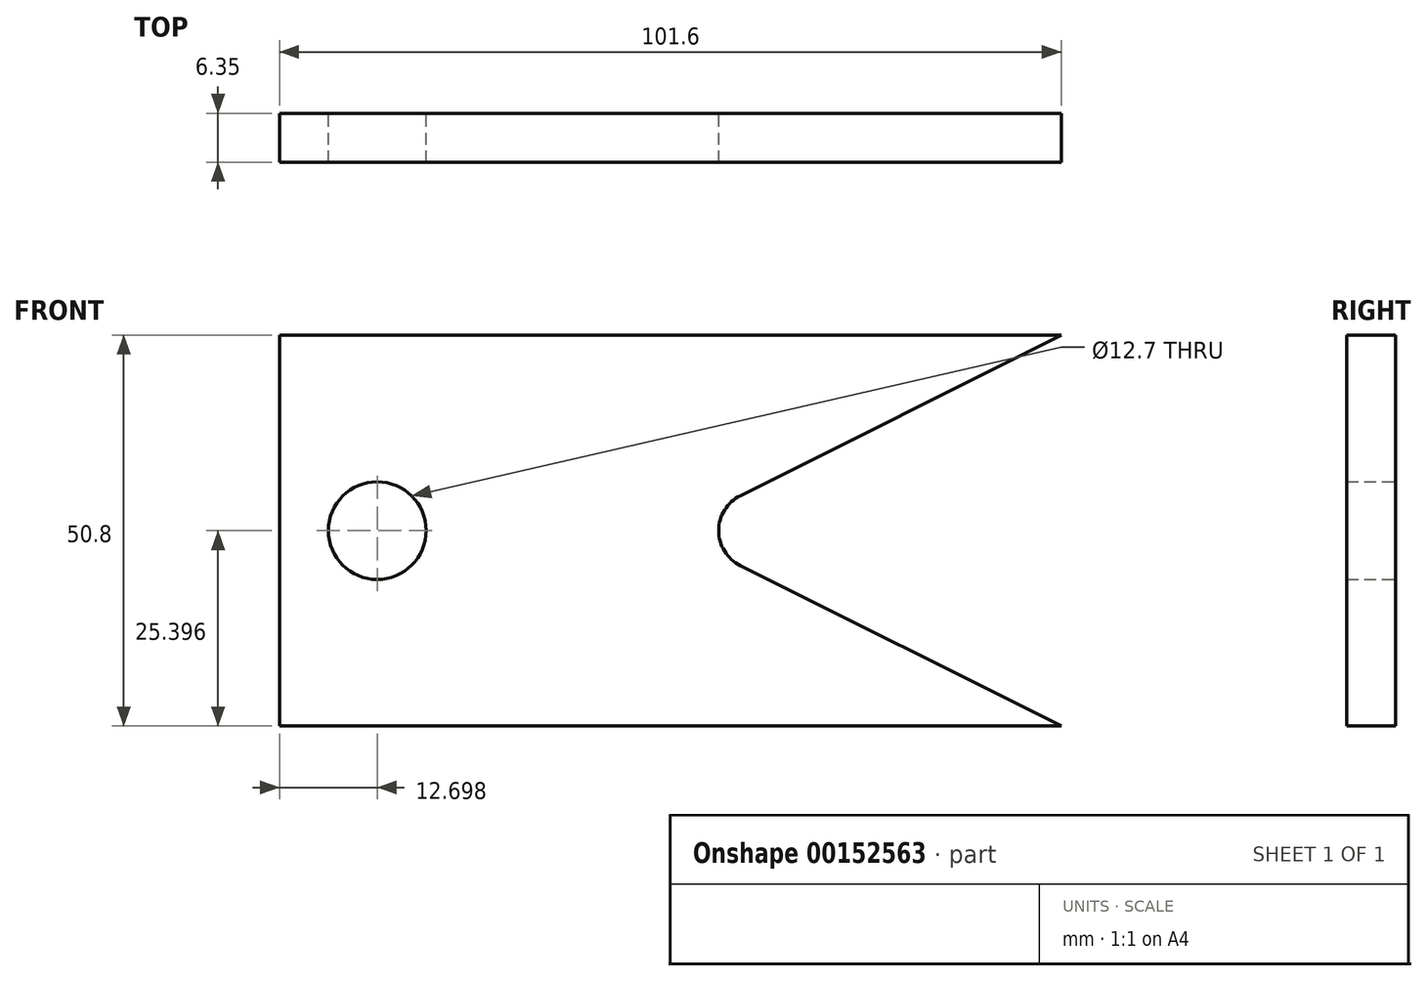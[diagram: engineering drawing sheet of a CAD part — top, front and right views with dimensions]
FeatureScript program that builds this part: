
annotation { "Feature Type Name" : "Feature", "Feature Type Description" : "" }
export const myFeature = defineFeature(function(context is Context, id is Id, definition is map)
    precondition{}
    {
        {
            var Q0;
            Q0=qCreatedBy(makeId("Front.planeOp"),FACE);
            var sketch = newSketch(context, id + "F0", { "sketchPlane" : qUnion([Q0])});
            skLineSegment(sketch, "E0.bottom", {"start": v(-46.68, 28.42) * mm, "end": v(54.92, 28.42) * mm});
            skLineSegment(sketch, "E0.top", {"start": v(-46.68, -22.38) * mm, "end": v(54.92, -22.38) * mm});
            skLineSegment(sketch, "E0.left", {"start": v(-46.68, 28.42) * mm, "end": v(-46.68, -22.38) * mm});
            skLineSegment(sketch, "E1", {"start": v(4.12, 3.02) * mm, "end": v(54.92, 28.42) * mm});
            skPoint(sketch, "E1.startSnap0", {"position": v(-46.68, 3.02) * mm});
            skPoint(sketch, "E1.startSnap1", {"position": v(4.12, 28.42) * mm});
            skLineSegment(sketch, "E2", {"start": v(4.12, 3.02) * mm, "end": v(54.92, -22.38) * mm});
            skCircle(sketch, "E3", {"center": v(-33.98, 3.02) * mm, "radius": 6.35 * mm});
            skSolve(sketch);
        }
        {
            var Q0;
            Q0 = qSketchRegion(id + "F0", true);
            extrude(context, id + "F1", {"entities" : qUnion([Q0]), "depth" : 6.35 * mm});
        }
        {
            var Q0;
            Q0=makeQuery(id+"F1.opExtrude","SWEPT_EDGE",EDGE,{"disambiguationData":[OSD([sQuery(id+"F0.wireOp",EDGE,"E1"),sQuery(id+"F0.wireOp",EDGE,"E2")])]});
            fillet(context, id + "F2", {"entities" : qUnion([Q0]), "radius" : 5.08 * mm, "tangentPropagation" : true, "allowEdgeOverflow" : false});
        }
    });
